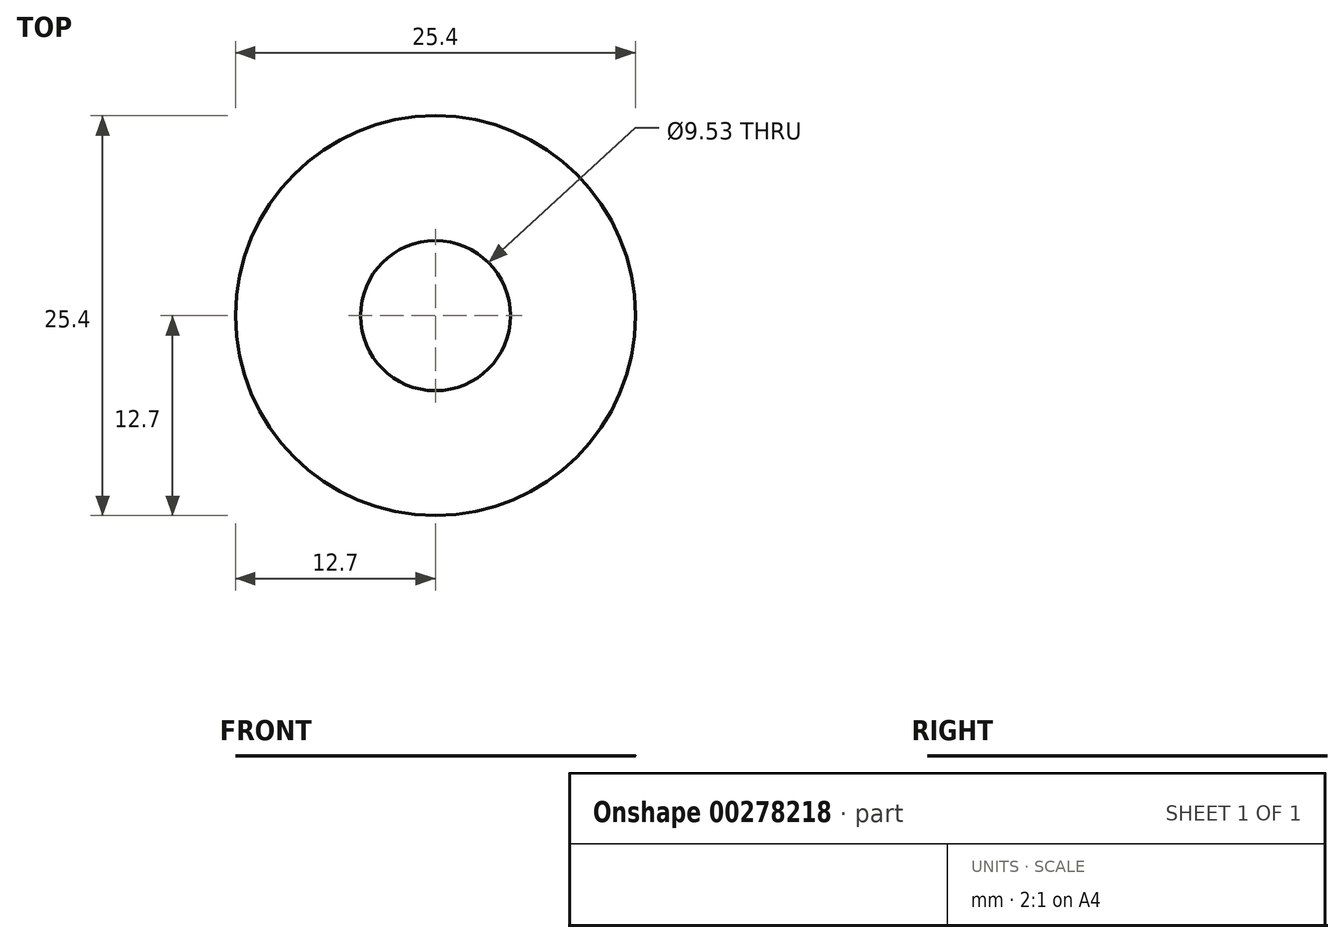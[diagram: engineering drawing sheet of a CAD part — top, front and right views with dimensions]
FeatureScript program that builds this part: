
annotation { "Feature Type Name" : "Feature", "Feature Type Description" : "" }
export const myFeature = defineFeature(function(context is Context, id is Id, definition is map)
    precondition{}
    {
        {
            var Q0;
            Q0=qCreatedBy(makeId("Top.planeOp"),FACE);
            var sketch = newSketch(context, id + "F0", { "sketchPlane" : qUnion([Q0])});
            skCircle(sketch, "E0", {"center": v(0, 0) * mm, "radius": 12.7 * mm});
            skCircle(sketch, "E1", {"center": v(0, 0) * mm, "radius": 4.76 * mm});
            skSolve(sketch);
        }
        {
            var Q0;
            Q0=makeQuery(id+"F0.imprint","IMPRINT",FACE,{"disambiguationData":[TD([[makeQuery(id+"F0.imprint","IMPRINT",EDGE,{"derivedFrom":sQuery(id+"F0.wireOp",EDGE,"E0")}),1.0]])]});
            extrude(context, id + "F1", {"entities" : qUnion([Q0]), "depth" : 1 / 203.2 * mm});
        }
    });
